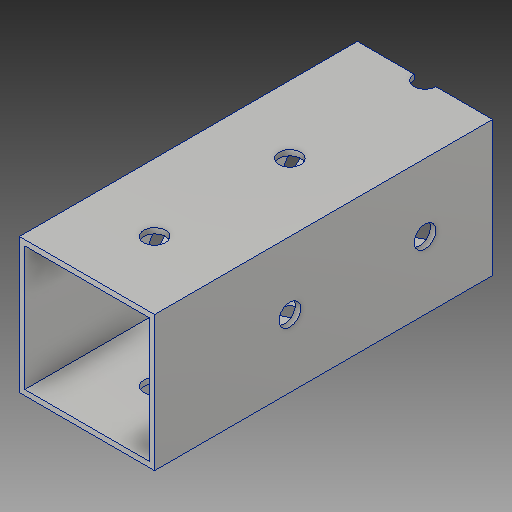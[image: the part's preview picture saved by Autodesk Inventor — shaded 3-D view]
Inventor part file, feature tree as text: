
AUTODESK INVENTOR PART (.ipt)
format: ipt  version: 2018 (Build 220112000, 112)  size: 150,528 bytes
history: native  units: in
note: dims shown in document units (in); Inventor stores cm internally (conversion verified against a paired STEP export)
features: other x5, sketch x3, hole x2, pattern_linear x2, projected_geometry x2, extrude x1
ambient origin geometry x8: Origin, YZ Plane, XZ Plane, XY Plane, X Axis, Y Axis, Z Axis, Center Point
bodies: Solid1 (feature_tree)
feature tree (15):
  other  "Table"
  other  "versatubing_1x1x40-"
  other  "versatubing_1x1x100-"
  other  "versatubing_1x2x100-"
  other  "versatubing_1x2ABS-"
  extrude  "Extrusion1"  Depth=1.0in
  hole  "Hole3"  [1 undecoded]
  hole  "Hole4"  [1 undecoded]
  pattern_linear  "Rectangular Pattern1"  Spacing1=1.0in  [1 undecoded]
  pattern_linear  "Rectangular Pattern2"  Spacing1=1.378in  [1 undecoded]
  sketch  "Sketch1"  dims[d4=0.0in d5=1.0in]
  sketch  "Sketch2"  dims[d6=0.5in d7=0.5in]
  projected_geometry  "Projected Loop1"
  sketch  "Sketch3"  dims[d22=1.0in d23=0.5in d24=1.0in d39=0.161in d40=0.75in d41=0.375in d42=0.25in d43=0.5635in d44=1.0in d45=0.8108in d46=0.161in d47=0.75in d48=0.375in d49=0.25in d50=0.5635in d51=1.0in d52=0.8108in d53=1.378in d55=1.0in d56=1.378in d58=1.0in]
  projected_geometry  "Projected Loop2"
note: 4 required parameter values undecoded (feature->parameter linkage not recoverable at this tier; creation-order binding heuristic only, values carry confidence <= 0.55)
